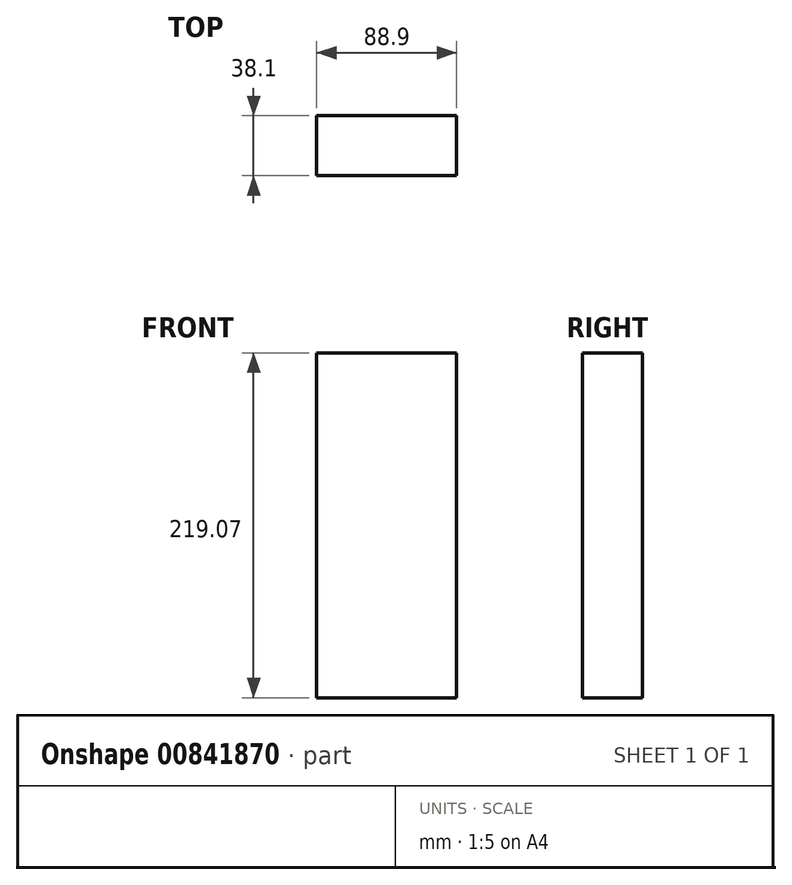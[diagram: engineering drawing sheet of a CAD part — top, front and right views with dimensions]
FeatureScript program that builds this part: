
annotation { "Feature Type Name" : "Feature", "Feature Type Description" : "" }
export const myFeature = defineFeature(function(context is Context, id is Id, definition is map)
    precondition{}
    {
        {
            var Q0;
            Q0=qCreatedBy(makeId("Top.planeOp"),FACE);
            var sketch = newSketch(context, id + "F0", { "sketchPlane" : qUnion([Q0])});
            skLineSegment(sketch, "E0.bottom", {"start": v(-44.45, 19.05) * mm, "end": v(44.45, 19.05) * mm});
            skLineSegment(sketch, "E0.top", {"start": v(-44.45, -19.05) * mm, "end": v(44.45, -19.05) * mm});
            skLineSegment(sketch, "E0.left", {"start": v(-44.45, 19.05) * mm, "end": v(-44.45, -19.05) * mm});
            skLineSegment(sketch, "E0.right", {"start": v(44.45, 19.05) * mm, "end": v(44.45, -19.05) * mm});
            skPoint(sketch, "E0.middle", {"position": v(0, 0) * mm});
            skSolve(sketch);
        }
        {
            var Q0;
            Q0=qSketchRegion(id+"F0",true);
            extrude(context, id + "F1", {"entities" : qUnion([Q0]), "depth" : 219.07 * mm, "offsetDistance" : 25.4 * mm});
        }
    });
